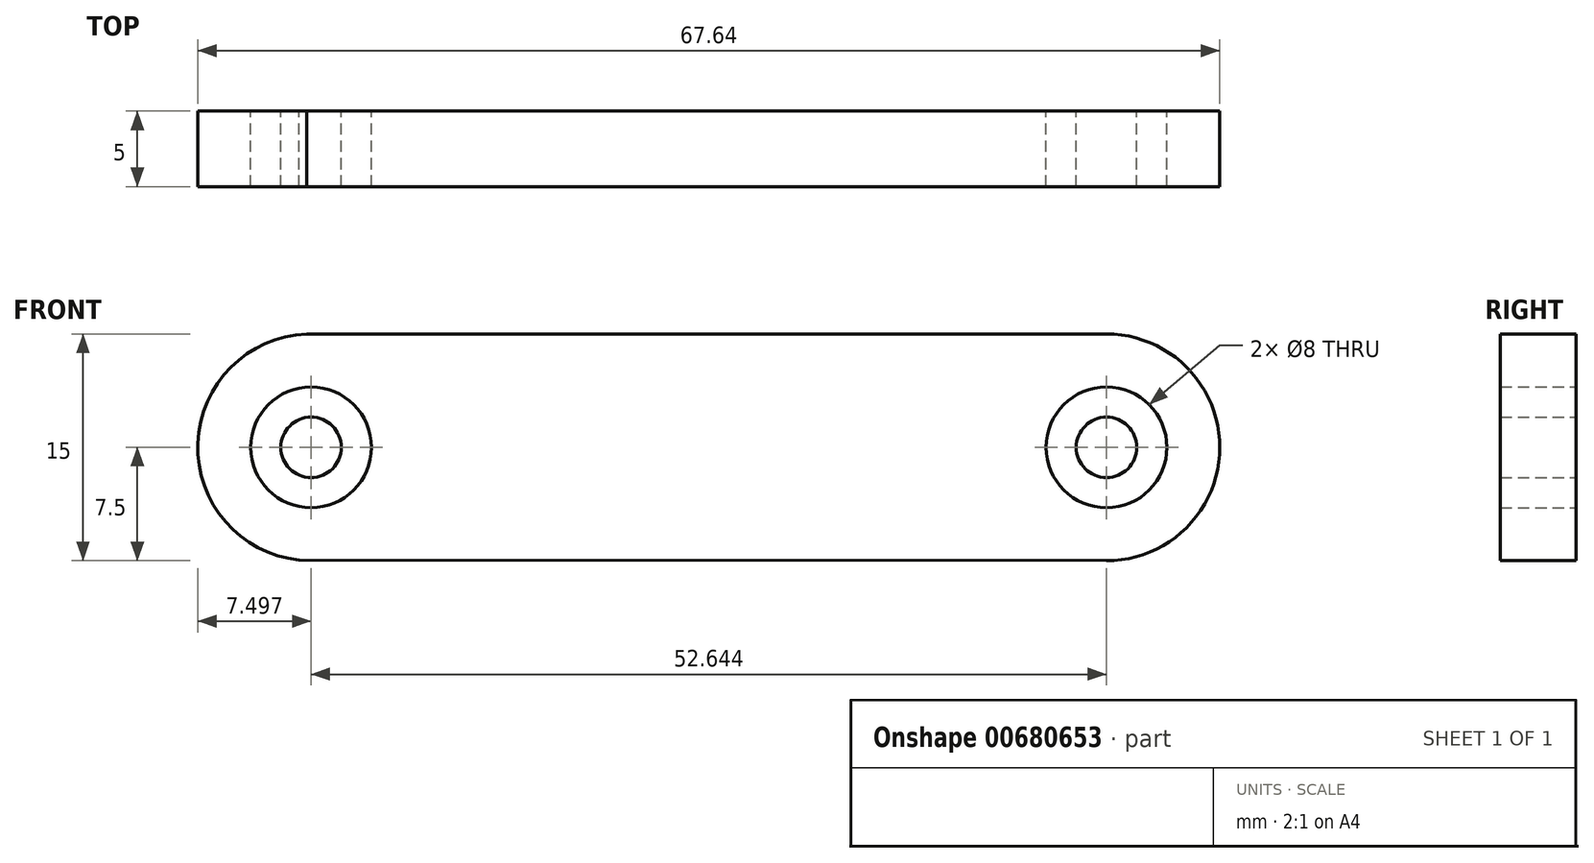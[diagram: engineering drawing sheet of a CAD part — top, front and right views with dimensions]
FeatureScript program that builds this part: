
annotation { "Feature Type Name" : "Feature", "Feature Type Description" : "" }
export const myFeature = defineFeature(function(context is Context, id is Id, definition is map)
    precondition{}
    {
        {
            var Q0;
            Q0=qCreatedBy(makeId("Front.planeOp"),FACE);
            var sketch = newSketch(context, id + "F0", { "sketchPlane" : qUnion([Q0])});
            skCircle(sketch, "E0", {"center": v(-16.9, 0) * mm, "radius": 4 * mm});
            skCircle(sketch, "E1", {"center": v(-16.9, 0) * mm, "radius": 2 * mm});
            skCircle(sketch, "E2", {"center": v(35.74, 0) * mm, "radius": 4 * mm});
            skCircle(sketch, "E3", {"center": v(35.74, 0) * mm, "radius": 2 * mm});
            skArc(sketch, "E4", {"start": v(-16.63, 7.5) * mm, "mid": v(-24.4, -0.26) * mm, "end": v(-16.12, -7.46) * mm});
            skArc(sketch, "E5", {"start": v(35.73, -7.5) * mm, "mid": v(43.24, 0) * mm, "end": v(35.74, 7.5) * mm});
            skLineSegment(sketch, "E6", {"start": v(-17.7, -7.46) * mm, "end": v(35.73, -7.5) * mm});
            skLineSegment(sketch, "E7", {"start": v(-17.18, 7.5) * mm, "end": v(35.74, 7.5) * mm});
            skSolve(sketch);
        }
        {
            var Q0;
            Q0=makeQuery(id+"F0.imprint","IMPRINT",FACE,{"disambiguationData":[TD([[makeQuery(id+"F0.imprint","IMPRINT",EDGE,{"derivedFrom":sQuery(id+"F0.wireOp",EDGE,"E0")}),-1.0]])]});
            var Q1;
            Q1=makeQuery(id+"F0.imprint","IMPRINT",FACE,{"disambiguationData":[TD([[makeQuery(id+"F0.imprint","IMPRINT",EDGE,{"derivedFrom":sQuery(id+"F0.wireOp",EDGE,"E3")}),1.0]])]});
            var Q2;
            Q2=makeQuery(id+"F0.imprint","IMPRINT",FACE,{"disambiguationData":[TD([[makeQuery(id+"F0.imprint","IMPRINT",EDGE,{"derivedFrom":sQuery(id+"F0.wireOp",EDGE,"E1")}),1.0]])]});
            extrude(context, id + "F1", {"entities" : qUnion([Q0, Q1, Q2]), "depth" : 5 * mm, "offsetDistance" : 25.4 * mm});
        }
    });
